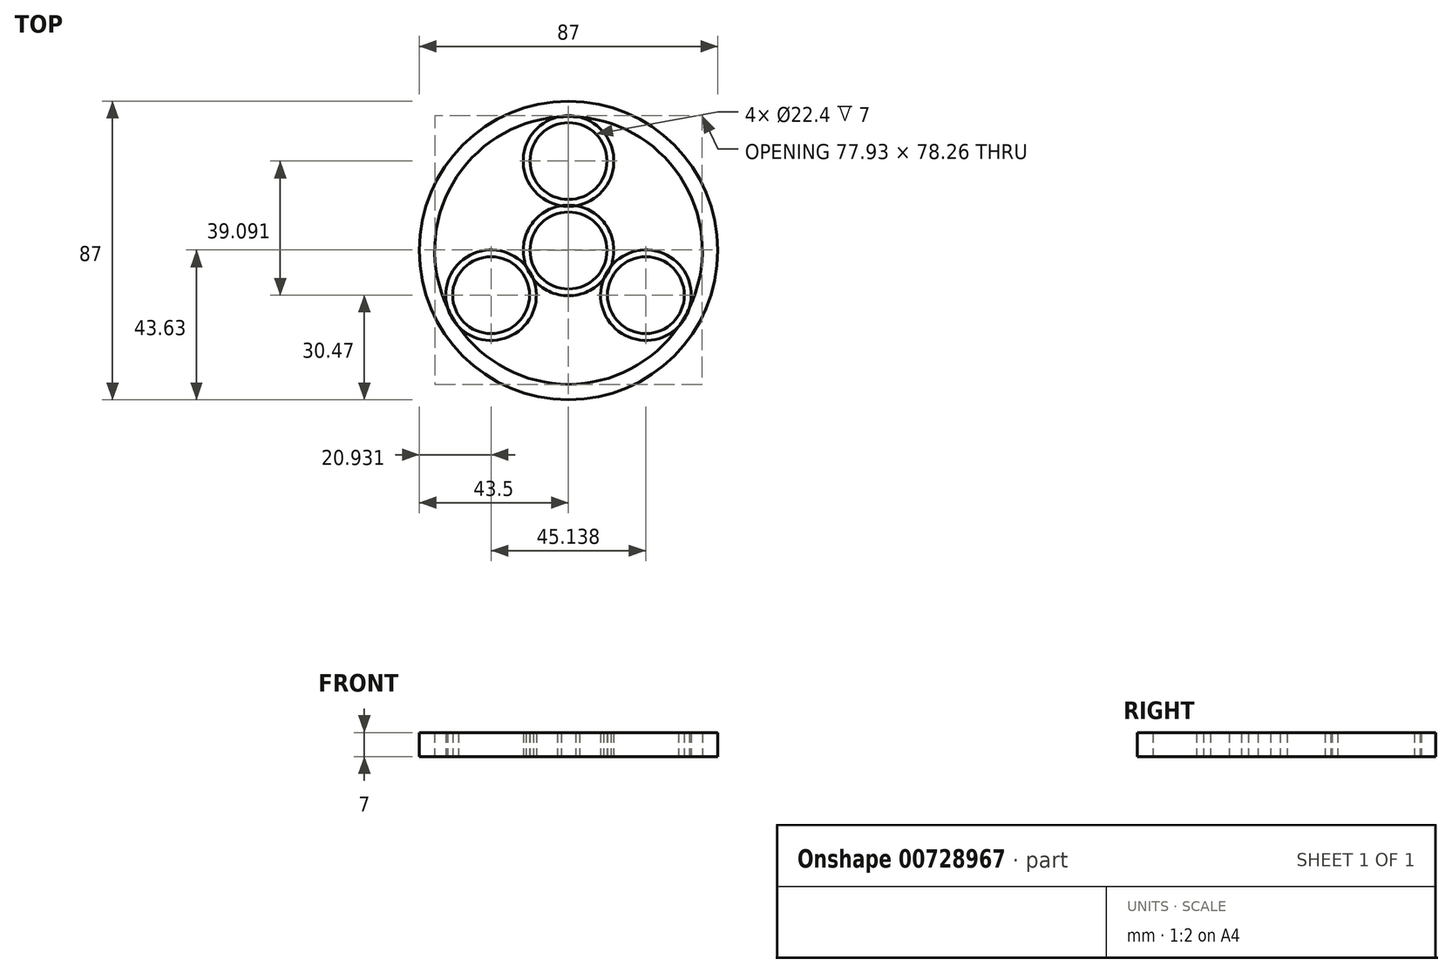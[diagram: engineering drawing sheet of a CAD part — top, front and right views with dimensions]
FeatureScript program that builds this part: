
annotation { "Feature Type Name" : "Feature", "Feature Type Description" : "" }
export const myFeature = defineFeature(function(context is Context, id is Id, definition is map)
    precondition{}
    {
        {
            var Q0;
            Q0=qCreatedBy(makeId("Top.planeOp"),FACE);
            var sketch = newSketch(context, id + "F0", { "sketchPlane" : qUnion([Q0])});
            skCircle(sketch, "E0", {"center": v(0, 0) * mm, "radius": 11.2 * mm});
            skCircle(sketch, "E1", {"center": v(0, 26.06) * mm, "radius": 11.2 * mm});
            skCircle(sketch, "E2", {"center": v(0, 0) * mm, "radius": 13.2 * mm});
            skCircle(sketch, "E3", {"center": v(0, 26.06) * mm, "radius": 13.2 * mm});
            skCircle(sketch, "E4.1.0", {"center": v(-22.57, -13.03) * mm, "radius": 13.2 * mm});
            skCircle(sketch, "E4.1.1", {"center": v(-22.57, -13.03) * mm, "radius": 11.2 * mm});
            skCircle(sketch, "E4.2.0", {"center": v(22.57, -13.03) * mm, "radius": 13.2 * mm});
            skCircle(sketch, "E4.2.1", {"center": v(22.57, -13.03) * mm, "radius": 11.2 * mm});
            skCircle(sketch, "E5", {"center": v(0, 0) * mm, "radius": 39 * mm});
            skCircle(sketch, "E6", {"center": v(0, 0) * mm, "radius": 43.5 * mm});
            skSolve(sketch);
        }
        {
            var Q0;
            Q0=makeQuery(id+"F0.imprint","IMPRINT",FACE,{"disambiguationData":[TD([[makeQuery(id+"F0.imprint","IMPRINT",EDGE,{"derivedFrom":sQuery(id+"F0.wireOp",EDGE,"E0")}),-1.0]])]});
            var Q1;
            Q1=makeQuery(id+"F0.imprint","IMPRINT",FACE,{"disambiguationData":[TD([[makeQuery(id+"F0.imprint","IMPRINT",EDGE,{"derivedFrom":sQuery(id+"F0.wireOp",EDGE,"E4.2.1")}),-1.0]])]});
            var Q2;
            Q2=makeQuery(id+"F0.imprint","IMPRINT",FACE,{"disambiguationData":[TD([[makeQuery(id+"F0.imprint","IMPRINT",EDGE,{"derivedFrom":sQuery(id+"F0.wireOp",EDGE,"E1")}),-1.0]])]});
            var Q3;
            Q3=makeQuery(id+"F0.imprint","IMPRINT",FACE,{"disambiguationData":[TD([[makeQuery(id+"F0.imprint","IMPRINT",EDGE,{"derivedFrom":sQuery(id+"F0.wireOp",EDGE,"E4.1.1")}),-1.0]])]});
            var Q4;
            Q4=makeQuery(id+"F0.imprint","IMPRINT",FACE,{"disambiguationData":[TD([[makeQuery(id+"F0.imprint","IMPRINT",EDGE,{"derivedFrom":sQuery(id+"F0.wireOp",EDGE,"E5")}),-1.0]])]});
            extrude(context, id + "F1", {"entities" : qUnion([Q0, Q1, Q2, Q3, Q4]), "depth" : 7 * mm, "offsetDistance" : 25 * mm});
        }
    });
